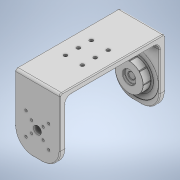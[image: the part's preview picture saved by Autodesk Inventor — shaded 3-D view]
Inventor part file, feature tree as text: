
AUTODESK INVENTOR PART (.ipt)
format: ipt  version: 2022 (Build 260153000, 153)  size: 537,088 bytes
history: native  units: mm
features: extrude x12, sketch x12, fillet x8, other x6, projected_geometry x3, mirror x1, pattern_circular x1, chamfer x1, revolve x1
ambient origin geometry x8: Origin, YZ Plane, XZ Plane, XY Plane, X Axis, Y Axis, Z Axis, Center Point
bodies: Body1 (feature_tree)
feature tree (45):
  other  "Твердое тело1"
  extrude  "Выдавливание1"  Depth=40.0mm
  extrude  "Выдавливание5"  Depth=93.4mm
  fillet  "Сопряжение3"  Radius=5.0mm
  other  "РабПлоскость1"
  extrude  "Выдавливание6"  Depth=45.8mm
  fillet  "Сопряжение4"  Radius=25.0mm
  fillet  "Сопряжение5"  Radius=3.0mm
  mirror  "Зеркальное отражение2"
  extrude  "Выдавливание7"  Depth=5.0mm
  other  "РабОсь6"
  extrude  "Выдавливание8"  Depth=55.0mm
  extrude  "Выдавливание9"  Depth=5.0mm TaperAngle=0.0deg
  extrude  "Выдавливание10"  Depth=5.0mm
  fillet  "Сопряжение7"  Radius=16.0mm
  other  "РабОсь1"
  pattern_circular  "Круговой массив1"  Count=4  [1 undecoded]
  fillet  "Сопряжение8"  Radius=7.0mm
  fillet  "Сопряжение11"  Radius=3.0mm
  other  "РабПлоскость3"
  extrude  "Выдавливание14"  Depth=37.8mm
  fillet  "Сопряжение14"  Radius=0.2mm
  extrude  "Выдавливание16"  Depth=24.7mm
  extrude  "Выдавливание17"  Depth=6.9mm TaperAngle=0.0deg
  fillet  "Сопряжение16"  Radius=0.5mm
  extrude  "Выдавливание18"  Depth=1.4mm TaperAngle=0.0deg
  chamfer  "Фаска2"  Distance=0.4mm
  other  "РабПлоскость4"
  revolve  "Вращение1"
  extrude  "Выдавливание19"  Depth=80.0mm TaperAngle=360.0deg
  sketch  "Эскиз1"
  sketch  "Эскиз5"
  sketch  "Эскиз6"
  sketch  "Эскиз7"
  projected_geometry  "Спроецированная петля1"
  sketch  "Эскиз9"
  sketch  "Эскиз10"
  sketch  "Эскиз17"
  sketch  "Эскиз19"
  sketch  "Эскиз20"
  projected_geometry  "Спроецированная петля3"
  sketch  "Эскиз21"
  sketch  "Эскиз22"
  sketch  "Эскиз23"
  projected_geometry  "Спроецированная петля4"
note: 1 required parameter value undecoded (feature->parameter linkage not recoverable at this tier; creation-order binding heuristic only, values carry confidence <= 0.55)
